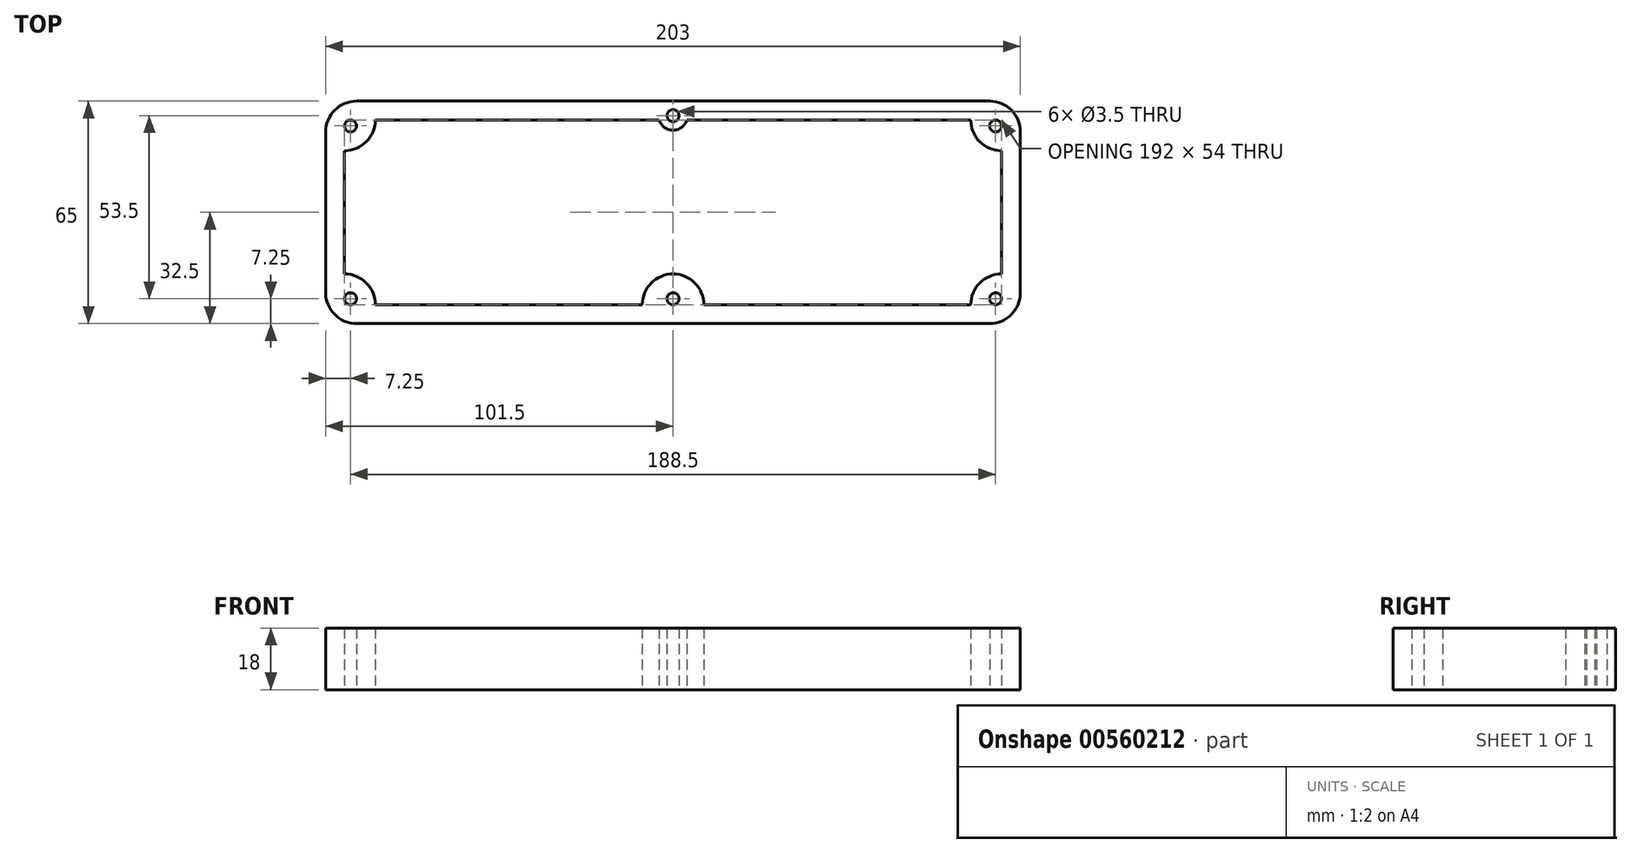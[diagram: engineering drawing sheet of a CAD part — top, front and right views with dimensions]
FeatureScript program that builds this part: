
annotation { "Feature Type Name" : "Feature", "Feature Type Description" : "" }
export const myFeature = defineFeature(function(context is Context, id is Id, definition is map)
    precondition{}
    {
        {
            var Q0;
            Q0=qCreatedBy(makeId("Top.planeOp"),FACE);
            var sketch = newSketch(context, id + "F0", { "sketchPlane" : qUnion([Q0])});
            skLineSegment(sketch, "E0.bottom", {"start": v(92.5, -32.5) * mm, "end": v(-92.5, -32.5) * mm});
            skLineSegment(sketch, "E0.top", {"start": v(92.5, 32.5) * mm, "end": v(-92.5, 32.5) * mm});
            skLineSegment(sketch, "E0.left", {"start": v(101.5, -23.5) * mm, "end": v(101.5, 23.5) * mm});
            skLineSegment(sketch, "E0.right", {"start": v(-101.5, -23.5) * mm, "end": v(-101.5, 23.5) * mm});
            skPoint(sketch, "E1.visualSharp", {"position": v(-101.5, 32.5) * mm});
            skArc(sketch, "E1.filletArc", {"start": v(-92.5, 32.5) * mm, "mid": v(-98.86, 29.86) * mm, "end": v(-101.5, 23.5) * mm});
            skPoint(sketch, "E2.visualSharp", {"position": v(-101.5, -32.5) * mm});
            skArc(sketch, "E2.filletArc", {"start": v(-101.5, -23.5) * mm, "mid": v(-98.86, -29.86) * mm, "end": v(-92.5, -32.5) * mm});
            skPoint(sketch, "E3.visualSharp", {"position": v(101.5, -32.5) * mm});
            skArc(sketch, "E3.filletArc", {"start": v(92.5, -32.5) * mm, "mid": v(98.86, -29.86) * mm, "end": v(101.5, -23.5) * mm});
            skPoint(sketch, "E4.visualSharp", {"position": v(101.5, 32.5) * mm});
            skArc(sketch, "E4.filletArc", {"start": v(101.5, 23.5) * mm, "mid": v(98.86, 29.86) * mm, "end": v(92.5, 32.5) * mm});
            skLineSegment(sketch, "E5.right", {"start": v(-96, -18) * mm, "end": v(-96, 18) * mm});
            skArc(sketch, "E6", {"start": v(-87, 27) * mm, "mid": v(-89.64, 20.64) * mm, "end": v(-96, 18) * mm});
            skCircle(sketch, "E7", {"center": v(-94.25, 25.25) * mm, "radius": 1.75 * mm});
            skPoint(sketch, "E8.orphan", {"position": v(-98.86, 29.86) * mm});
            skPoint(sketch, "E9.orphan", {"position": v(-89.64, 20.64) * mm});
            skCircle(sketch, "E10.MirrorC", {"center": v(94.25, 25.25) * mm, "radius": 1.75 * mm});
            skCircle(sketch, "E11.MirrorC", {"center": v(-94.25, -25.25) * mm, "radius": 1.75 * mm});
            skArc(sketch, "E12.MirrorCS", {"start": v(-87, -27) * mm, "mid": v(-89.64, -20.64) * mm, "end": v(-96, -18) * mm});
            skCircle(sketch, "E13.MirrorC", {"center": v(94.25, -25.25) * mm, "radius": 1.75 * mm});
            skArc(sketch, "E14.MirrorCS", {"start": v(87, 27) * mm, "mid": v(89.64, 20.64) * mm, "end": v(96, 18) * mm});
            skArc(sketch, "E15.MirrorCS", {"start": v(87, -27) * mm, "mid": v(89.64, -20.64) * mm, "end": v(96, -18) * mm});
            skLineSegment(sketch, "E16.trimOffspring", {"start": v(87, -27) * mm, "end": v(9, -27) * mm});
            skLineSegment(sketch, "E17.trimOffspring", {"start": v(96, -18) * mm, "end": v(96, 18) * mm});
            skPoint(sketch, "E18.endSnap0", {"position": v(0, -32.5) * mm});
            skArc(sketch, "E19.MirrorCS", {"start": v(-9, -27) * mm, "mid": v(0, -18) * mm, "end": v(9, -27) * mm});
            skCircle(sketch, "E20.MirrorC", {"center": v(0, -25.25) * mm, "radius": 1.75 * mm});
            skLineSegment(sketch, "E21.trimOffspring", {"start": v(-9, -27) * mm, "end": v(-87, -27) * mm});
            skLineSegment(sketch, "E22", {"start": v(-87, 27) * mm, "end": v(-4.06, 27) * mm});
            skCircle(sketch, "E23", {"center": v(0, 28.25) * mm, "radius": 1.75 * mm});
            skArc(sketch, "E24", {"start": v(-4.06, 27) * mm, "mid": v(0, 24) * mm, "end": v(4.06, 27) * mm});
            skLineSegment(sketch, "E25.trimOffspring", {"start": v(4.06, 27) * mm, "end": v(87, 27) * mm});
            skSolve(sketch);
        }
        {
            var Q0;
            Q0 = qSketchRegion(id + "F0", true);
            extrude(context, id + "F1", {"entities" : qUnion([Q0]), "depth" : 18 * mm, "offsetDistance" : 25 * mm});
        }
    });
